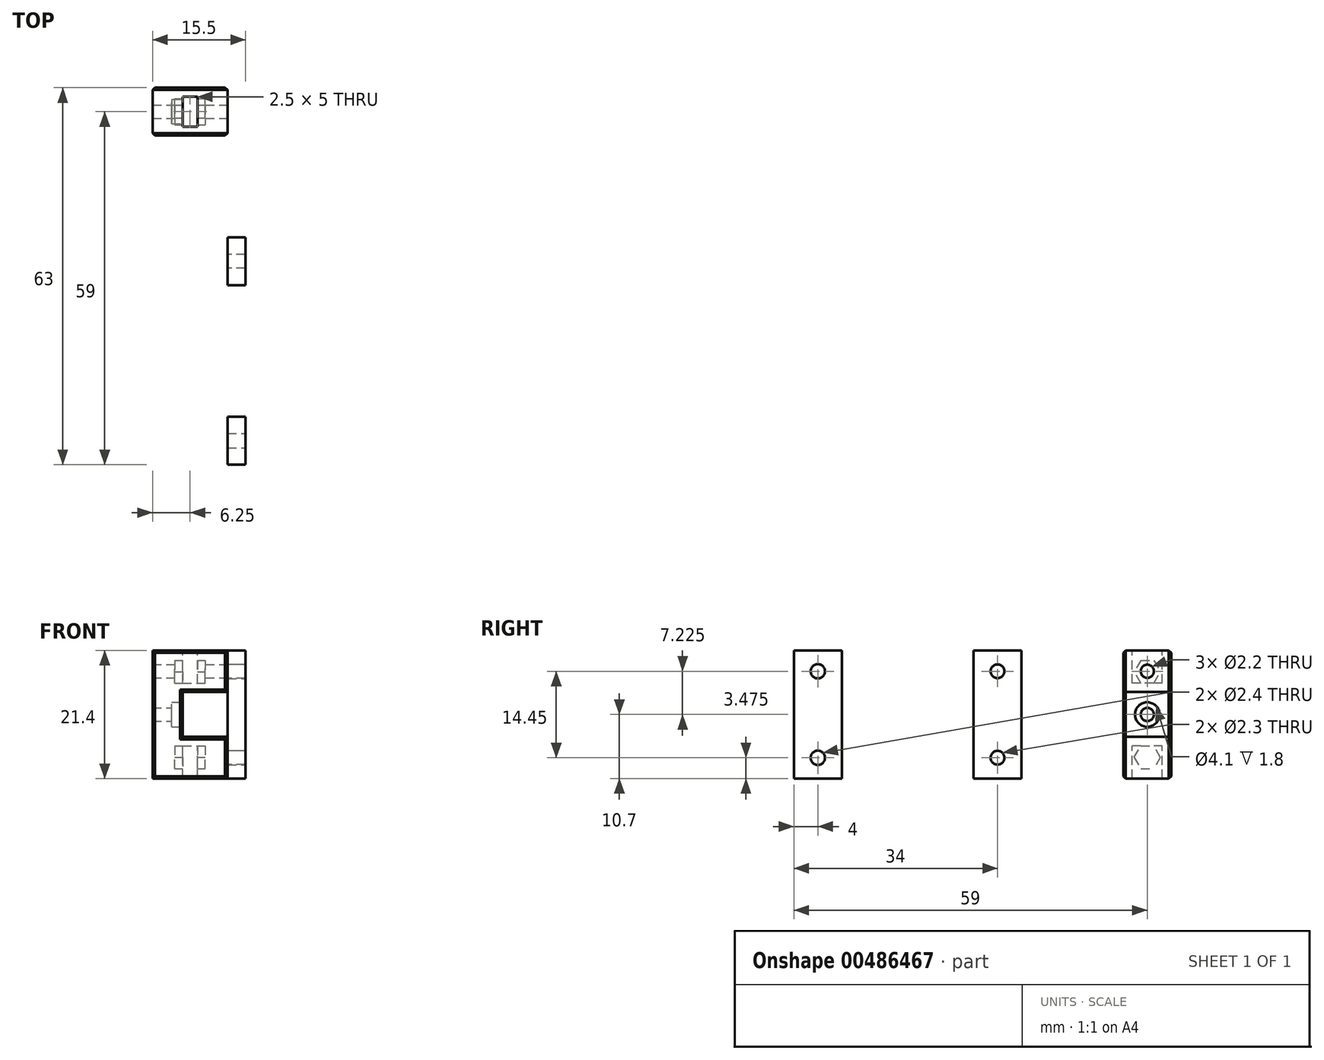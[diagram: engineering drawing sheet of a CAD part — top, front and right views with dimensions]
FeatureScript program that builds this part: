
annotation { "Feature Type Name" : "Feature", "Feature Type Description" : "" }
export const myFeature = defineFeature(function(context is Context, id is Id, definition is map)
    precondition{}
    {
        {
            assignVariable(context, id + "F0", {"name" : "nut_distance", "anyValue" : 5 * mm});
        }
        {
            var Q0;
            Q0=qCreatedBy(makeId("Front.planeOp"),FACE);
            var sketch = newSketch(context, id + "F1", { "sketchPlane" : qUnion([Q0])});
            skLineSegment(sketch, "E0", {"start": v(0, 3.75) * mm, "end": v(-7.5, 3.75) * mm});
            skLineSegment(sketch, "E1", {"start": v(-7.5, -3.75) * mm, "end": v(-7.5, 3.75) * mm});
            skLineSegment(sketch, "E2", {"start": v(-7.5, -3.75) * mm, "end": v(0, -3.75) * mm});
            skLineSegment(sketch, "E3", {"start": v(0, -10.7) * mm, "end": v(0, -3.75) * mm});
            skLineSegment(sketch, "E4", {"start": v(0, -10.7) * mm, "end": v(-12.5, -10.7) * mm});
            skLineSegment(sketch, "E5", {"start": v(-12.5, -10.7) * mm, "end": v(-12.5, 10.7) * mm});
            skLineSegment(sketch, "E6", {"start": v(0, 3.75) * mm, "end": v(0, 10.7) * mm});
            skLineSegment(sketch, "E7", {"start": v(-12.5, 10.7) * mm, "end": v(0, 10.7) * mm});
            skSolve(sketch);
        }
        {
            var Q0;
            Q0=qSketchRegion(id+"F1",true);
            extrude(context, id + "F2", {"entities" : qUnion([Q0]), "depth" : 8 * mm, "offsetDistance" : 25 * mm, "symmetric" : true});
        }
        {
            var Q0;
            Q0=makeQuery(id+"F2.opExtrude","SWEPT_FACE",FACE,{"disambiguationData":[OSD([sQuery(id+"F1.wireOp",EDGE,"E6")])]});
            var sketch = newSketch(context, id + "F3", { "sketchPlane" : qUnion([Q0])});
            skLineSegment(sketch, "E8", {"start": v(-12.42, 0) * mm, "end": v(17.97, 0) * mm, "construction": true});
            skLineSegment(sketch, "E9", {"start": v(0, 22.03) * mm, "end": v(0, -15.29) * mm, "construction": true});
            skPoint(sketch, "E9.startSnap0", {"position": v(0, 10.7) * mm});
            skLineSegment(sketch, "E10", {"start": v(0, 5.25) * mm, "end": v(-1.1, 5.25) * mm});
            skLineSegment(sketch, "E11", {"start": v(-1.1, 5.25) * mm, "end": v(-2.2, 7.15) * mm});
            skLineSegment(sketch, "E12", {"start": v(-2.2, 7.15) * mm, "end": v(0, 7.15) * mm, "construction": true});
            skLineSegment(sketch, "E13", {"start": v(0, 7.15) * mm, "end": v(1.1, 5.25) * mm, "construction": true});
            skLineSegment(sketch, "E14.MirrorCS", {"start": v(-1.1, 9.05) * mm, "end": v(-2.2, 7.15) * mm});
            skLineSegment(sketch, "E15.MirrorCS", {"start": v(0, 9.05) * mm, "end": v(-1.1, 9.05) * mm});
            skLineSegment(sketch, "E16.MirrorCS", {"start": v(0, 9.05) * mm, "end": v(1.1, 9.05) * mm});
            skLineSegment(sketch, "E17.MirrorCS", {"start": v(1.1, 9.05) * mm, "end": v(2.2, 7.15) * mm});
            skLineSegment(sketch, "E18.MirrorCS", {"start": v(1.1, 5.25) * mm, "end": v(2.2, 7.15) * mm});
            skLineSegment(sketch, "E19.MirrorCS", {"start": v(0, 5.25) * mm, "end": v(1.1, 5.25) * mm});
            skLineSegment(sketch, "E20.MirrorCS", {"start": v(-1.1, -9.05) * mm, "end": v(-2.2, -7.15) * mm});
            skLineSegment(sketch, "E21.MirrorCS", {"start": v(0, -9.05) * mm, "end": v(-1.1, -9.05) * mm});
            skLineSegment(sketch, "E22.MirrorCS", {"start": v(0, -9.05) * mm, "end": v(1.1, -9.05) * mm});
            skLineSegment(sketch, "E23.MirrorCS", {"start": v(1.1, -9.05) * mm, "end": v(2.2, -7.15) * mm});
            skLineSegment(sketch, "E24.MirrorCS", {"start": v(1.1, -5.25) * mm, "end": v(2.2, -7.15) * mm});
            skLineSegment(sketch, "E25.MirrorCS", {"start": v(0, -5.25) * mm, "end": v(1.1, -5.25) * mm});
            skLineSegment(sketch, "E26.MirrorCS", {"start": v(0, -5.25) * mm, "end": v(-1.1, -5.25) * mm});
            skLineSegment(sketch, "E27.MirrorCS", {"start": v(-1.1, -5.25) * mm, "end": v(-2.2, -7.15) * mm});
            skSolve(sketch);
        }
        {
            var Q0;
            Q0=makeQuery(id+"F3.imprint","IMPRINT",FACE,{"disambiguationData":[TD([[makeQuery(id+"F3.imprint","IMPRINT",EDGE,{"derivedFrom":sQuery(id+"F3.wireOp",EDGE,"E10")}),-1.0]])]});
            var Q1;
            Q1=makeQuery(id+"F3.imprint","IMPRINT",FACE,{"disambiguationData":[TD([[makeQuery(id+"F3.imprint","IMPRINT",EDGE,{"derivedFrom":sQuery(id+"F3.wireOp",EDGE,"E20.MirrorCS")}),-1.0]])]});
            extrude(context, id + "F4", {"entities" : qUnion([Q0, Q1]), "operationType" : NewBodyOperationType.REMOVE, "oppositeDirection" : true, "depth" : 5.4 * mm, "hasOffset" : true, "offsetDistance" : 4 * mm, "hasSecondDirection" : true, "secondDirectionOppositeDirection" : true, "secondDirectionDepth" : getVariable(context, 'nut_distance') - 1.3 * mm});
        }
        {
            var Q0;
            Q0=makeQuery(id+"F2.opExtrude","SWEPT_FACE",FACE,{"disambiguationData":[OSD([sQuery(id+"F1.wireOp",EDGE,"E7")])]});
            var sketch = newSketch(context, id + "F5", { "sketchPlane" : qUnion([Q0])});
            skLineSegment(sketch, "E28.bottom", {"start": v(-7.5, 2.5) * mm, "end": v(-5, 2.5) * mm});
            skLineSegment(sketch, "E28.top", {"start": v(-7.5, -2.5) * mm, "end": v(-5, -2.5) * mm});
            skLineSegment(sketch, "E28.left", {"start": v(-7.5, 2.5) * mm, "end": v(-7.5, -2.5) * mm});
            skLineSegment(sketch, "E28.right", {"start": v(-5, 2.5) * mm, "end": v(-5, -2.5) * mm});
            skSolve(sketch);
        }
        {
            var Q0;
            Q0=qSketchRegion(id+"F5",true);
            var Q1;
            Q1=makeQuery(id+"F4.boolean.opBoolean","COPY",VERTEX,{"derivedFrom":makeQuery(id+"F4.opExtrude","CAP_VERTEX",VERTEX,{"disambiguationData":[OSD([sQuery(id+"F3.wireOp",EDGE,"E10"),sQuery(id+"F3.wireOp",EDGE,"E11")])],"isStart":false})});
            extrude(context, id + "F6", {"entities" : qUnion([Q0]), "operationType" : NewBodyOperationType.REMOVE, "endBound" : BoundingType.UP_TO_VERTEX, "oppositeDirection" : true, "depth" : 25 * mm, "endBoundEntityVertex" : qUnion([Q1]), "offsetDistance" : 25 * mm});
        }
        {
            var Q0;
            Q0=makeQuery(id+"F2.opExtrude","SWEPT_FACE",FACE,{"disambiguationData":[OSD([sQuery(id+"F1.wireOp",EDGE,"E6")])]});
            var sketch = newSketch(context, id + "F7", { "sketchPlane" : qUnion([Q0])});
            skCircle(sketch, "E29", {"center": v(0, 7.22) * mm, "radius": 1.1 * mm});
            skCircle(sketch, "E30.MirrorC", {"center": v(0, -7.22) * mm, "radius": 1.1 * mm});
            skSolve(sketch);
        }
        {
            var Q0;
            Q0=makeQuery(id+"F7.imprint","IMPRINT",FACE,{"disambiguationData":[TD([[makeQuery(id+"F7.imprint","IMPRINT",EDGE,{"derivedFrom":sQuery(id+"F7.wireOp",EDGE,"E29")}),1.0]])]});
            var Q1;
            Q1=makeQuery(id+"F7.imprint","IMPRINT",FACE,{"disambiguationData":[TD([[makeQuery(id+"F7.imprint","IMPRINT",EDGE,{"derivedFrom":sQuery(id+"F7.wireOp",EDGE,"E30.MirrorC")}),-1.0]])]});
            var Q2;
            Q2=makeQuery(id+"F4.boolean.opBoolean","COPY",VERTEX,{"derivedFrom":makeQuery(id+"F4.opExtrude","CAP_VERTEX",VERTEX,{"disambiguationData":[OSD([sQuery(id+"F3.wireOp",EDGE,"E17.MirrorCS"),sQuery(id+"F3.wireOp",EDGE,"E18.MirrorCS")])],"isStart":false})});
            extrude(context, id + "F8", {"entities" : qUnion([Q0, Q1]), "operationType" : NewBodyOperationType.REMOVE, "endBound" : BoundingType.THROUGH_ALL, "oppositeDirection" : true, "depth" : 25 * mm, "endBoundEntityVertex" : qUnion([Q2]), "offsetDistance" : 25 * mm});
        }
        {
            var Q0;
            Q0=qSketchRegion(id+"F5",true);
            var Q1;
            Q1=makeQuery(id+"F2.opExtrude","SWEPT_FACE",FACE,{"disambiguationData":[OSD([sQuery(id+"F1.wireOp",EDGE,"E4")])]});
            var Q2;
            Q2=makeQuery(id+"F4.boolean.opBoolean","COPY",VERTEX,{"derivedFrom":makeQuery(id+"F4.opExtrude","CAP_VERTEX",VERTEX,{"disambiguationData":[OSD([sQuery(id+"F3.wireOp",EDGE,"E26.MirrorCS"),sQuery(id+"F3.wireOp",EDGE,"E27.MirrorCS")])],"isStart":false})});
            extrude(context, id + "F9", {"entities" : qUnion([Q0]), "operationType" : NewBodyOperationType.REMOVE, "endBound" : BoundingType.UP_TO_SURFACE, "oppositeDirection" : true, "depth" : 25 * mm, "endBoundEntityFace" : qUnion([Q1]), "offsetDistance" : 25 * mm, "hasSecondDirection" : true, "secondDirectionBound" : BoundingType.UP_TO_VERTEX, "secondDirectionOppositeDirection" : true, "secondDirectionDepth" : 25 * mm, "secondDirectionBoundEntityVertex" : qUnion([Q2])});
        }
        {
            var Q0;
            Q0=qSketchRegion(id+"F3",true);
            extrude(context, id + "F10", {"entities" : qUnion([Q0]), "operationType" : NewBodyOperationType.REMOVE, "oppositeDirection" : true, "depth" : (7.5 + 1.3) * mm, "offsetDistance" : 25 * mm, "hasSecondDirection" : true, "secondDirectionOppositeDirection" : true, "secondDirectionDepth" : (5.4 + 1.7) * mm});
        }
        {
            var Q0;
            Q0=makeQuery(id+"F2.opExtrude","SWEPT_FACE",FACE,{"disambiguationData":[OSD([sQuery(id+"F1.wireOp",EDGE,"E1")])]});
            var sketch = newSketch(context, id + "F11", { "sketchPlane" : qUnion([Q0])});
            skCircle(sketch, "E31", {"center": v(0, 0) * mm, "radius": 1.1 * mm});
            skSolve(sketch);
        }
        {
            var Q0;
            Q0=makeQuery(id+"F11.imprint","IMPRINT",FACE,{"disambiguationData":[TD([[makeQuery(id+"F11.imprint","IMPRINT",EDGE,{"derivedFrom":sQuery(id+"F11.wireOp",EDGE,"E31")}),-1.0]])]});
            var sketch = newSketch(context, id + "F12", { "sketchPlane" : qUnion([Q0])});
            skCircle(sketch, "E32", {"center": v(0, 0) * mm, "radius": 2.05 * mm});
            skSolve(sketch);
        }
        {
            var Q0;
            Q0=qSketchRegion(id+"F11",true);
            extrude(context, id + "F13", {"entities" : qUnion([Q0]), "operationType" : NewBodyOperationType.REMOVE, "endBound" : BoundingType.UP_TO_NEXT, "oppositeDirection" : true, "depth" : 25 * mm, "offsetDistance" : 25 * mm});
        }
        {
            var Q0;
            Q0=qSketchRegion(id+"F12",true);
            extrude(context, id + "F14", {"entities" : qUnion([Q0]), "operationType" : NewBodyOperationType.REMOVE, "oppositeDirection" : true, "depth" : 1.8 * mm, "offsetDistance" : 25 * mm});
        }
        {
            var Q0;
            Q0=qCreatedBy(makeId("Front.planeOp"),FACE);
            cPlane(context, id + "F15", {"entities" : qUnion([Q0]), "cplaneType" : CPlaneType.OFFSET, "offset" : 25 * mm, "width" : 150 * mm, "height" : 150 * mm});
        }
        {
            var Q0;
            Q0=qCreatedBy(makeId("Right.planeOp"),FACE);
            var sketch = newSketch(context, id + "F16", { "sketchPlane" : qUnion([Q0])});
            skLineSegment(sketch, "E33.bottom", {"start": v(-21, 10.7) * mm, "end": v(-29, 10.7) * mm});
            skLineSegment(sketch, "E33.top", {"start": v(-21, -10.7) * mm, "end": v(-29, -10.7) * mm});
            skLineSegment(sketch, "E33.left", {"start": v(-21, 10.7) * mm, "end": v(-21, -10.7) * mm});
            skLineSegment(sketch, "E33.right", {"start": v(-29, 10.7) * mm, "end": v(-29, -10.7) * mm});
            skCircle(sketch, "E34", {"center": v(-25, 7.22) * mm, "radius": 1.15 * mm});
            skCircle(sketch, "E35.MirrorC", {"center": v(-25, -7.22) * mm, "radius": 1.15 * mm});
            skSolve(sketch);
        }
        {
            var Q0;
            Q0=makeQuery(id+"F16.imprint","IMPRINT",FACE,{"disambiguationData":[TD([[makeQuery(id+"F16.imprint","IMPRINT",EDGE,{"derivedFrom":sQuery(id+"F16.wireOp",EDGE,"E33.bottom")}),1.0]])]});
            extrude(context, id + "F17", {"entities" : qUnion([Q0]), "depth" : 3 * mm, "offsetDistance" : 25 * mm});
        }
        {
            var Q0;
            Q0=qCreatedBy(id+"F15.planeOp",FACE);
            var sketch = newSketch(context, id + "F18", { "sketchPlane" : qUnion([Q0])});
            skArc(sketch, "E36", {"start": v(0, 3.75) * mm, "mid": v(-0.1, 0) * mm, "end": v(0, -3.75) * mm});
            skLineSegment(sketch, "E37", {"start": v(0, 3.75) * mm, "end": v(0, -3.75) * mm});
            skSolve(sketch);
        }
        {
            var Q0;
            Q0=makeQuery(id+"F17.opExtrude","SWEPT_BODY",BODY,{"disambiguationData":[OSD([sQuery(id+"F16.wireOp",EDGE,"E33.bottom"),sQuery(id+"F16.wireOp",EDGE,"E33.top"),sQuery(id+"F16.wireOp",EDGE,"E33.left"),sQuery(id+"F16.wireOp",EDGE,"E33.right"),sQuery(id+"F16.wireOp",EDGE,"E34"),sQuery(id+"F16.wireOp",EDGE,"E35.MirrorC")])]});
            transform(context, id + "F19", {"entities" : qUnion([Q0]), "transformType" : TransformType.TRANSLATION_3D, "dx" : 0 * mm, "dy" : -30 * mm, "dz" : 0 * mm, "makeCopy" : true});
        }
        {
            var Q0;
            Q0=makeQuery(id+"F19.opPattern","COPY",FACE,{"derivedFrom":makeQuery(id+"F17.opExtrude","CAP_FACE",FACE,{"disambiguationData":[OSD([sQuery(id+"F16.wireOp",EDGE,"E33.bottom"),sQuery(id+"F16.wireOp",EDGE,"E33.top"),sQuery(id+"F16.wireOp",EDGE,"E33.left"),sQuery(id+"F16.wireOp",EDGE,"E33.right"),sQuery(id+"F16.wireOp",EDGE,"E34"),sQuery(id+"F16.wireOp",EDGE,"E35.MirrorC")])],"isStart":false}),"instanceName":"1"});
            var sketch = newSketch(context, id + "F20", { "sketchPlane" : qUnion([Q0])});
            skCircle(sketch, "E38", {"center": v(-55, 7.22) * mm, "radius": 1.2 * mm});
            skCircle(sketch, "E39.MirrorC", {"center": v(-55, -7.22) * mm, "radius": 1.2 * mm});
            skSolve(sketch);
        }
        {
            var Q0;
            Q0=qSketchRegion(id+"F20",true);
            extrude(context, id + "F21", {"entities" : qUnion([Q0]), "operationType" : NewBodyOperationType.REMOVE, "endBound" : BoundingType.THROUGH_ALL, "oppositeDirection" : true, "depth" : 25 * mm, "offsetDistance" : 25 * mm});
        }
        {
            var Q0;
            Q0=makeQuery(id+"F2.opExtrude","CAP_EDGE",EDGE,{"disambiguationData":[OSD([sQuery(id+"F1.wireOp",EDGE,"E1")])],"isStart":false});
            var Q1;
            Q1=makeQuery(id+"F2.opExtrude","CAP_EDGE",EDGE,{"disambiguationData":[OSD([sQuery(id+"F1.wireOp",EDGE,"E0")])],"isStart":false});
            var Q2;
            Q2=makeQuery(id+"F2.opExtrude","CAP_EDGE",EDGE,{"disambiguationData":[OSD([sQuery(id+"F1.wireOp",EDGE,"E2")])],"isStart":false});
            var Q3;
            Q3=makeQuery(id+"F2.opExtrude","CAP_EDGE",EDGE,{"disambiguationData":[OSD([sQuery(id+"F1.wireOp",EDGE,"E0")])],"isStart":true});
            var Q4;
            Q4=makeQuery(id+"F2.opExtrude","CAP_EDGE",EDGE,{"disambiguationData":[OSD([sQuery(id+"F1.wireOp",EDGE,"E1")])],"isStart":true});
            var Q5;
            Q5=makeQuery(id+"F2.opExtrude","CAP_EDGE",EDGE,{"disambiguationData":[OSD([sQuery(id+"F1.wireOp",EDGE,"E2")])],"isStart":true});
            var Q6;
            Q6=makeQuery(id+"F2.opExtrude","CAP_EDGE",EDGE,{"disambiguationData":[OSD([sQuery(id+"F1.wireOp",EDGE,"E6")])],"isStart":false});
            var Q7;
            Q7=makeQuery(id+"F2.opExtrude","CAP_EDGE",EDGE,{"disambiguationData":[OSD([sQuery(id+"F1.wireOp",EDGE,"E6")])],"isStart":true});
            var Q8;
            Q8=makeQuery(id+"F2.opExtrude","CAP_EDGE",EDGE,{"disambiguationData":[OSD([sQuery(id+"F1.wireOp",EDGE,"E7")])],"isStart":true});
            var Q9;
            Q9=makeQuery(id+"F2.opExtrude","CAP_EDGE",EDGE,{"disambiguationData":[OSD([sQuery(id+"F1.wireOp",EDGE,"E7")])],"isStart":false});
            var Q10;
            Q10=makeQuery(id+"F2.opExtrude","CAP_EDGE",EDGE,{"disambiguationData":[OSD([sQuery(id+"F1.wireOp",EDGE,"E5")])],"isStart":false});
            var Q11;
            Q11=makeQuery(id+"F2.opExtrude","CAP_EDGE",EDGE,{"disambiguationData":[OSD([sQuery(id+"F1.wireOp",EDGE,"E5")])],"isStart":true});
            var Q12;
            Q12=makeQuery(id+"F2.opExtrude","CAP_EDGE",EDGE,{"disambiguationData":[OSD([sQuery(id+"F1.wireOp",EDGE,"E4")])],"isStart":true});
            var Q13;
            Q13=makeQuery(id+"F2.opExtrude","CAP_EDGE",EDGE,{"disambiguationData":[OSD([sQuery(id+"F1.wireOp",EDGE,"E3")])],"isStart":true});
            var Q14;
            Q14=makeQuery(id+"F2.opExtrude","CAP_EDGE",EDGE,{"disambiguationData":[OSD([sQuery(id+"F1.wireOp",EDGE,"E3")])],"isStart":false});
            var Q15;
            Q15=makeQuery(id+"F2.opExtrude","CAP_EDGE",EDGE,{"disambiguationData":[OSD([sQuery(id+"F1.wireOp",EDGE,"E4")])],"isStart":false});
            chamfer(context, id + "F22", {"entities" : qUnion([Q0, Q1, Q2, Q3, Q4, Q5, Q6, Q7, Q8, Q9, Q10, Q11, Q12, Q13, Q14, Q15]), "width" : 0.4 * mm, "tangentPropagation" : true});
        }
    });
